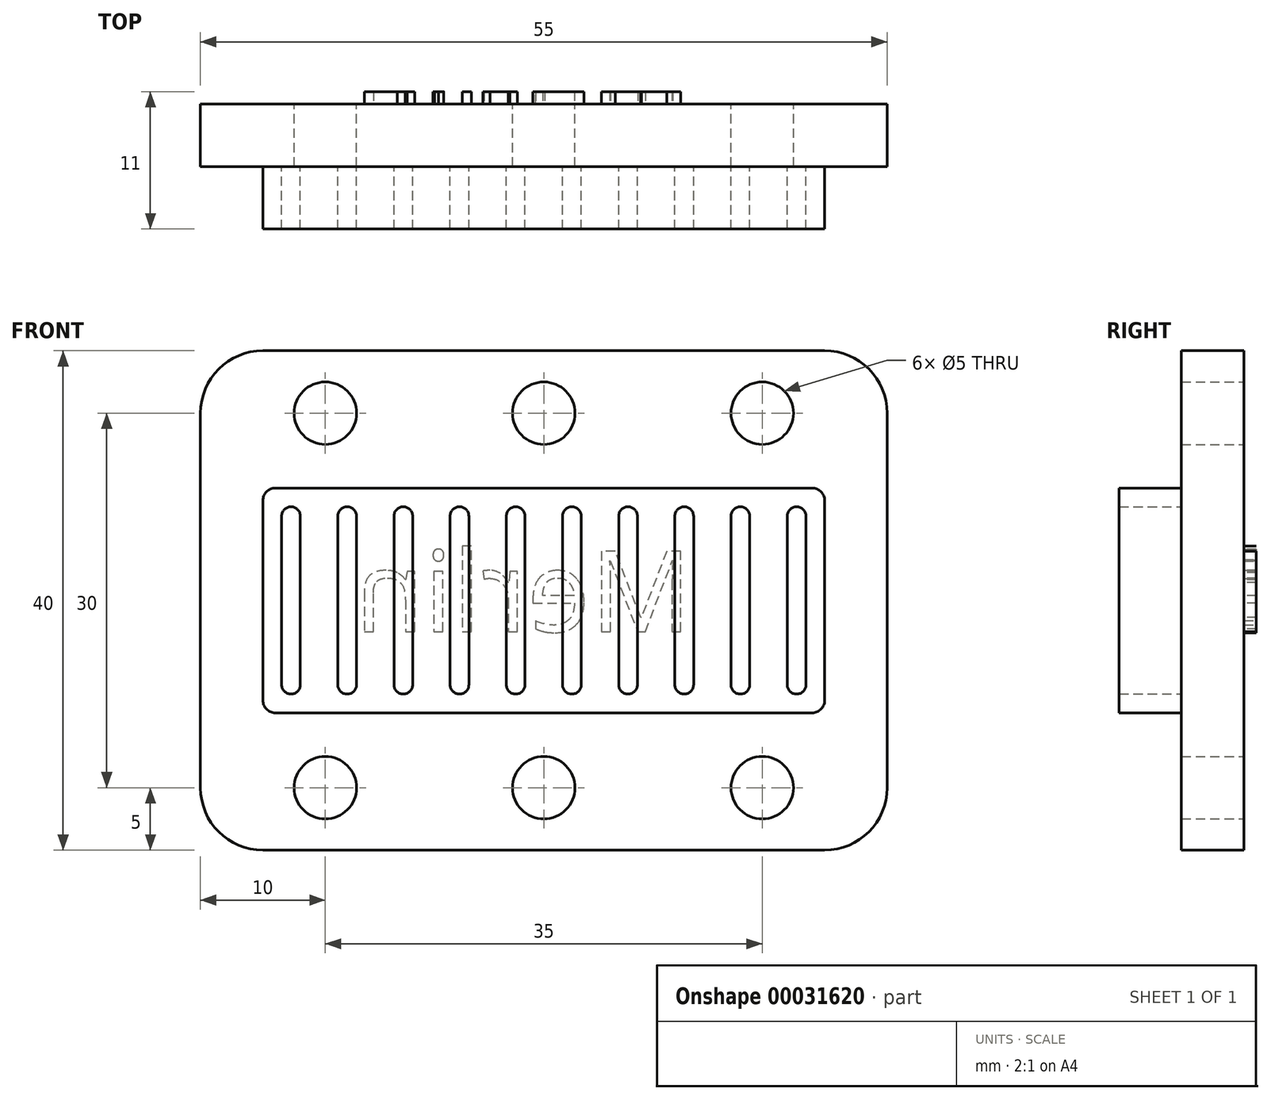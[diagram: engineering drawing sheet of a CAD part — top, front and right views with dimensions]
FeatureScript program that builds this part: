
annotation { "Feature Type Name" : "Feature", "Feature Type Description" : "" }
export const myFeature = defineFeature(function(context is Context, id is Id, definition is map)
    precondition{}
    {
        {
            var Q0;
            Q0=qCreatedBy(makeId("Front.planeOp"),FACE);
            var sketch = newSketch(context, id + "F0", { "sketchPlane" : qUnion([Q0])});
            skLineSegment(sketch, "E0.bottom", {"start": v(-5, 0) * mm, "end": v(-50, 0) * mm});
            skLineSegment(sketch, "E0.top", {"start": v(-5, 40) * mm, "end": v(-50, 40) * mm});
            skLineSegment(sketch, "E0.left", {"start": v(0, 5) * mm, "end": v(0, 35) * mm});
            skLineSegment(sketch, "E0.right", {"start": v(-55, 5) * mm, "end": v(-55, 35) * mm});
            skCircle(sketch, "E1", {"center": v(-45, 35) * mm, "radius": 2.5 * mm});
            skLineSegment(sketch, "E2", {"start": v(-67.85, 20) * mm, "end": v(10.82, 20) * mm, "construction": true});
            skCircle(sketch, "E3.MirrorC", {"center": v(-45, 5) * mm, "radius": 2.5 * mm});
            skCircle(sketch, "E4", {"center": v(-27.5, 35) * mm, "radius": 2.5 * mm});
            skCircle(sketch, "E5", {"center": v(-10, 35) * mm, "radius": 2.5 * mm});
            skCircle(sketch, "E6.MirrorC", {"center": v(-27.5, 5) * mm, "radius": 2.5 * mm});
            skCircle(sketch, "E7.MirrorC", {"center": v(-10, 5) * mm, "radius": 2.5 * mm});
            skPoint(sketch, "E8.visualSharp", {"position": v(-55, 40) * mm});
            skArc(sketch, "E8.filletArc", {"start": v(-50, 40) * mm, "mid": v(-53.54, 38.54) * mm, "end": v(-55, 35) * mm});
            skPoint(sketch, "E9.visualSharp", {"position": v(-55, 0) * mm});
            skArc(sketch, "E9.filletArc", {"start": v(-55, 5) * mm, "mid": v(-53.54, 1.46) * mm, "end": v(-50, 0) * mm});
            skPoint(sketch, "E10.visualSharp", {"position": v(0, 0) * mm});
            skArc(sketch, "E10.filletArc", {"start": v(-5, 0) * mm, "mid": v(-1.46, 1.46) * mm, "end": v(0, 5) * mm});
            skPoint(sketch, "E11.visualSharp", {"position": v(0, 40) * mm});
            skArc(sketch, "E11.filletArc", {"start": v(0, 35) * mm, "mid": v(-1.46, 38.54) * mm, "end": v(-5, 40) * mm});
            skSolve(sketch);
        }
        {
            var Q0;
            Q0 = qSketchRegion(id + "F0", true);
            extrude(context, id + "F1", {"entities" : qUnion([Q0]), "depth" : 5 * mm});
        }
        {
            var Q0;
            Q0=makeQuery(id+"F1.opExtrude","CAP_FACE",FACE,{"disambiguationData":[OSD([sQuery(id+"F0.wireOp",EDGE,"E0.bottom"),sQuery(id+"F0.wireOp",EDGE,"E0.top"),sQuery(id+"F0.wireOp",EDGE,"E0.left"),sQuery(id+"F0.wireOp",EDGE,"E0.right"),sQuery(id+"F0.wireOp",EDGE,"E1"),sQuery(id+"F0.wireOp",EDGE,"E3.MirrorC"),sQuery(id+"F0.wireOp",EDGE,"E4"),sQuery(id+"F0.wireOp",EDGE,"E5"),sQuery(id+"F0.wireOp",EDGE,"E6.MirrorC"),sQuery(id+"F0.wireOp",EDGE,"E7.MirrorC"),sQuery(id+"F0.wireOp",EDGE,"E8.filletArc"),sQuery(id+"F0.wireOp",EDGE,"E9.filletArc"),sQuery(id+"F0.wireOp",EDGE,"E10.filletArc"),sQuery(id+"F0.wireOp",EDGE,"E11.filletArc")])],"isStart":true});
            var sketch = newSketch(context, id + "F2", { "sketchPlane" : qUnion([Q0])});
            skText(sketch, "E12", { "text": "Merlin", "fontName": "OpenSans-Regular.ttf"});
            const initialGuessF2  = {"E12": [0.01564, 0.0175, 1, 0, 0.00649]};
            skSetInitialGuess(sketch, initialGuessF2);
            skSolve(sketch);
        }
        {
            var Q0;
            Q0 = qSketchRegion(id + "F2", true);
            extrude(context, id + "F3", {"entities" : qUnion([Q0]), "operationType" : NewBodyOperationType.ADD, "depth" : 1 * mm});
        }
        {
            var Q0;
            Q0=makeQuery(id+"F1.opExtrude","CAP_FACE",FACE,{"disambiguationData":[OSD([sQuery(id+"F0.wireOp",EDGE,"E0.bottom"),sQuery(id+"F0.wireOp",EDGE,"E0.top"),sQuery(id+"F0.wireOp",EDGE,"E0.left"),sQuery(id+"F0.wireOp",EDGE,"E0.right"),sQuery(id+"F0.wireOp",EDGE,"E1"),sQuery(id+"F0.wireOp",EDGE,"E3.MirrorC"),sQuery(id+"F0.wireOp",EDGE,"E4"),sQuery(id+"F0.wireOp",EDGE,"E5"),sQuery(id+"F0.wireOp",EDGE,"E6.MirrorC"),sQuery(id+"F0.wireOp",EDGE,"E7.MirrorC"),sQuery(id+"F0.wireOp",EDGE,"E8.filletArc"),sQuery(id+"F0.wireOp",EDGE,"E9.filletArc"),sQuery(id+"F0.wireOp",EDGE,"E10.filletArc"),sQuery(id+"F0.wireOp",EDGE,"E11.filletArc")])],"isStart":false});
            var sketch = newSketch(context, id + "F4", { "sketchPlane" : qUnion([Q0])});
            skLineSegment(sketch, "E13.bottom", {"start": v(-49, 29) * mm, "end": v(-6, 29) * mm});
            skLineSegment(sketch, "E13.top", {"start": v(-49, 11) * mm, "end": v(-6, 11) * mm});
            skLineSegment(sketch, "E13.left", {"start": v(-50, 28) * mm, "end": v(-50, 12) * mm});
            skLineSegment(sketch, "E13.right", {"start": v(-5, 28) * mm, "end": v(-5, 12) * mm});
            skLineSegment(sketch, "E14.bottom", {"start": v(-47.75, 27.5) * mm, "end": v(-47.75, 27.5) * mm});
            skLineSegment(sketch, "E14.top", {"start": v(-47.75, 12.5) * mm, "end": v(-47.75, 12.5) * mm});
            skLineSegment(sketch, "E14.left", {"start": v(-48.5, 26.75) * mm, "end": v(-48.5, 13.25) * mm});
            skLineSegment(sketch, "E14.right", {"start": v(-47, 26.75) * mm, "end": v(-47, 13.25) * mm});
            skPoint(sketch, "E15.visualSharp", {"position": v(-5, 29) * mm});
            skArc(sketch, "E15.filletArc", {"start": v(-5, 28) * mm, "mid": v(-5.3, 28.7) * mm, "end": v(-6, 29) * mm});
            skPoint(sketch, "E16.visualSharp", {"position": v(-5, 11) * mm});
            skArc(sketch, "E16.filletArc", {"start": v(-6, 11) * mm, "mid": v(-5.3, 11.3) * mm, "end": v(-5, 12) * mm});
            skPoint(sketch, "E17.visualSharp", {"position": v(-50, 11) * mm});
            skArc(sketch, "E17.filletArc", {"start": v(-50, 12) * mm, "mid": v(-49.7, 11.3) * mm, "end": v(-49, 11) * mm});
            skPoint(sketch, "E18.visualSharp", {"position": v(-50, 29) * mm});
            skArc(sketch, "E18.filletArc", {"start": v(-49, 29) * mm, "mid": v(-49.7, 28.7) * mm, "end": v(-50, 28) * mm});
            skPoint(sketch, "E19.visualSharp", {"position": v(-47, 27.5) * mm});
            skArc(sketch, "E19.filletArc", {"start": v(-47, 26.75) * mm, "mid": v(-47.22, 27.28) * mm, "end": v(-47.75, 27.5) * mm});
            skPoint(sketch, "E20.visualSharp", {"position": v(-48.5, 27.5) * mm});
            skArc(sketch, "E20.filletArc", {"start": v(-47.75, 27.5) * mm, "mid": v(-48.28, 27.28) * mm, "end": v(-48.5, 26.75) * mm});
            skPoint(sketch, "E21.visualSharp", {"position": v(-48.5, 12.5) * mm});
            skArc(sketch, "E21.filletArc", {"start": v(-48.5, 13.25) * mm, "mid": v(-48.28, 12.72) * mm, "end": v(-47.75, 12.5) * mm});
            skPoint(sketch, "E22.visualSharp", {"position": v(-47, 12.5) * mm});
            skArc(sketch, "E22.filletArc", {"start": v(-47.75, 12.5) * mm, "mid": v(-47.22, 12.72) * mm, "end": v(-47, 13.25) * mm});
            skLineSegment(sketch, "E23.1.0.0", {"start": v(-44, 26.75) * mm, "end": v(-44, 13.25) * mm});
            skArc(sketch, "E23.1.0.1", {"start": v(-43.25, 27.5) * mm, "mid": v(-43.78, 27.28) * mm, "end": v(-44, 26.75) * mm});
            skArc(sketch, "E23.1.0.2", {"start": v(-42.5, 26.75) * mm, "mid": v(-42.72, 27.28) * mm, "end": v(-43.25, 27.5) * mm});
            skLineSegment(sketch, "E23.1.0.3", {"start": v(-42.5, 26.75) * mm, "end": v(-42.5, 13.25) * mm});
            skArc(sketch, "E23.1.0.4", {"start": v(-43.25, 12.5) * mm, "mid": v(-42.72, 12.72) * mm, "end": v(-42.5, 13.25) * mm});
            skArc(sketch, "E23.1.0.5", {"start": v(-44, 13.25) * mm, "mid": v(-43.78, 12.72) * mm, "end": v(-43.25, 12.5) * mm});
            skLineSegment(sketch, "E23.2.0.0", {"start": v(-39.5, 26.75) * mm, "end": v(-39.5, 13.25) * mm});
            skArc(sketch, "E23.2.0.1", {"start": v(-38.75, 27.5) * mm, "mid": v(-39.28, 27.28) * mm, "end": v(-39.5, 26.75) * mm});
            skArc(sketch, "E23.2.0.2", {"start": v(-38, 26.75) * mm, "mid": v(-38.22, 27.28) * mm, "end": v(-38.75, 27.5) * mm});
            skLineSegment(sketch, "E23.2.0.3", {"start": v(-38, 26.75) * mm, "end": v(-38, 13.25) * mm});
            skArc(sketch, "E23.2.0.4", {"start": v(-38.75, 12.5) * mm, "mid": v(-38.22, 12.72) * mm, "end": v(-38, 13.25) * mm});
            skArc(sketch, "E23.2.0.5", {"start": v(-39.5, 13.25) * mm, "mid": v(-39.28, 12.72) * mm, "end": v(-38.75, 12.5) * mm});
            skLineSegment(sketch, "E23.direction1", {"start": v(-48.5, 13.25) * mm, "end": v(-44, 13.25) * mm, "construction": true});
            skLineSegment(sketch, "E24.0.3.0", {"start": v(-35, 26.75) * mm, "end": v(-35, 13.25) * mm});
            skArc(sketch, "E24.3.3.0", {"start": v(-34.25, 27.5) * mm, "mid": v(-34.78, 27.28) * mm, "end": v(-35, 26.75) * mm});
            skArc(sketch, "E24.7.3.0", {"start": v(-33.5, 26.75) * mm, "mid": v(-33.72, 27.28) * mm, "end": v(-34.25, 27.5) * mm});
            skLineSegment(sketch, "E24.11.3.0", {"start": v(-33.5, 26.75) * mm, "end": v(-33.5, 13.25) * mm});
            skArc(sketch, "E24.14.3.0", {"start": v(-34.25, 12.5) * mm, "mid": v(-33.72, 12.72) * mm, "end": v(-33.5, 13.25) * mm});
            skArc(sketch, "E24.18.3.0", {"start": v(-35, 13.25) * mm, "mid": v(-34.78, 12.72) * mm, "end": v(-34.25, 12.5) * mm});
            skLineSegment(sketch, "E24.0.4.0", {"start": v(-30.5, 26.75) * mm, "end": v(-30.5, 13.25) * mm});
            skArc(sketch, "E24.3.4.0", {"start": v(-29.75, 27.5) * mm, "mid": v(-30.28, 27.28) * mm, "end": v(-30.5, 26.75) * mm});
            skArc(sketch, "E24.7.4.0", {"start": v(-29, 26.75) * mm, "mid": v(-29.22, 27.28) * mm, "end": v(-29.75, 27.5) * mm});
            skLineSegment(sketch, "E24.11.4.0", {"start": v(-29, 26.75) * mm, "end": v(-29, 13.25) * mm});
            skArc(sketch, "E24.14.4.0", {"start": v(-29.75, 12.5) * mm, "mid": v(-29.22, 12.72) * mm, "end": v(-29, 13.25) * mm});
            skArc(sketch, "E24.18.4.0", {"start": v(-30.5, 13.25) * mm, "mid": v(-30.28, 12.72) * mm, "end": v(-29.75, 12.5) * mm});
            skLineSegment(sketch, "E24.0.5.0", {"start": v(-26, 26.75) * mm, "end": v(-26, 13.25) * mm});
            skArc(sketch, "E24.3.5.0", {"start": v(-25.25, 27.5) * mm, "mid": v(-25.78, 27.28) * mm, "end": v(-26, 26.75) * mm});
            skArc(sketch, "E24.7.5.0", {"start": v(-24.5, 26.75) * mm, "mid": v(-24.72, 27.28) * mm, "end": v(-25.25, 27.5) * mm});
            skLineSegment(sketch, "E24.11.5.0", {"start": v(-24.5, 26.75) * mm, "end": v(-24.5, 13.25) * mm});
            skArc(sketch, "E24.14.5.0", {"start": v(-25.25, 12.5) * mm, "mid": v(-24.72, 12.72) * mm, "end": v(-24.5, 13.25) * mm});
            skArc(sketch, "E24.18.5.0", {"start": v(-26, 13.25) * mm, "mid": v(-25.78, 12.72) * mm, "end": v(-25.25, 12.5) * mm});
            skLineSegment(sketch, "E24.0.6.0", {"start": v(-21.5, 26.75) * mm, "end": v(-21.5, 13.25) * mm});
            skArc(sketch, "E24.3.6.0", {"start": v(-20.75, 27.5) * mm, "mid": v(-21.28, 27.28) * mm, "end": v(-21.5, 26.75) * mm});
            skArc(sketch, "E24.7.6.0", {"start": v(-20, 26.75) * mm, "mid": v(-20.22, 27.28) * mm, "end": v(-20.75, 27.5) * mm});
            skLineSegment(sketch, "E24.11.6.0", {"start": v(-20, 26.75) * mm, "end": v(-20, 13.25) * mm});
            skArc(sketch, "E24.14.6.0", {"start": v(-20.75, 12.5) * mm, "mid": v(-20.22, 12.72) * mm, "end": v(-20, 13.25) * mm});
            skArc(sketch, "E24.18.6.0", {"start": v(-21.5, 13.25) * mm, "mid": v(-21.28, 12.72) * mm, "end": v(-20.75, 12.5) * mm});
            skLineSegment(sketch, "E24.0.7.0", {"start": v(-17, 26.75) * mm, "end": v(-17, 13.25) * mm});
            skArc(sketch, "E24.3.7.0", {"start": v(-16.25, 27.5) * mm, "mid": v(-16.78, 27.28) * mm, "end": v(-17, 26.75) * mm});
            skArc(sketch, "E24.7.7.0", {"start": v(-15.5, 26.75) * mm, "mid": v(-15.72, 27.28) * mm, "end": v(-16.25, 27.5) * mm});
            skLineSegment(sketch, "E24.11.7.0", {"start": v(-15.5, 26.75) * mm, "end": v(-15.5, 13.25) * mm});
            skArc(sketch, "E24.14.7.0", {"start": v(-16.25, 12.5) * mm, "mid": v(-15.72, 12.72) * mm, "end": v(-15.5, 13.25) * mm});
            skArc(sketch, "E24.18.7.0", {"start": v(-17, 13.25) * mm, "mid": v(-16.78, 12.72) * mm, "end": v(-16.25, 12.5) * mm});
            skLineSegment(sketch, "E24.0.8.0", {"start": v(-12.5, 26.75) * mm, "end": v(-12.5, 13.25) * mm});
            skArc(sketch, "E24.3.8.0", {"start": v(-11.75, 27.5) * mm, "mid": v(-12.28, 27.28) * mm, "end": v(-12.5, 26.75) * mm});
            skArc(sketch, "E24.7.8.0", {"start": v(-11, 26.75) * mm, "mid": v(-11.22, 27.28) * mm, "end": v(-11.75, 27.5) * mm});
            skLineSegment(sketch, "E24.11.8.0", {"start": v(-11, 26.75) * mm, "end": v(-11, 13.25) * mm});
            skArc(sketch, "E24.14.8.0", {"start": v(-11.75, 12.5) * mm, "mid": v(-11.22, 12.72) * mm, "end": v(-11, 13.25) * mm});
            skArc(sketch, "E24.18.8.0", {"start": v(-12.5, 13.25) * mm, "mid": v(-12.28, 12.72) * mm, "end": v(-11.75, 12.5) * mm});
            skLineSegment(sketch, "E24.0.9.0", {"start": v(-8, 26.75) * mm, "end": v(-8, 13.25) * mm});
            skArc(sketch, "E24.3.9.0", {"start": v(-7.25, 27.5) * mm, "mid": v(-7.78, 27.28) * mm, "end": v(-8, 26.75) * mm});
            skArc(sketch, "E24.7.9.0", {"start": v(-6.5, 26.75) * mm, "mid": v(-6.72, 27.28) * mm, "end": v(-7.25, 27.5) * mm});
            skLineSegment(sketch, "E24.11.9.0", {"start": v(-6.5, 26.75) * mm, "end": v(-6.5, 13.25) * mm});
            skArc(sketch, "E24.14.9.0", {"start": v(-7.25, 12.5) * mm, "mid": v(-6.72, 12.72) * mm, "end": v(-6.5, 13.25) * mm});
            skArc(sketch, "E24.18.9.0", {"start": v(-8, 13.25) * mm, "mid": v(-7.78, 12.72) * mm, "end": v(-7.25, 12.5) * mm});
            skSolve(sketch);
        }
        {
            var Q0;
            Q0 = qSketchRegion(id + "F4", true);
            extrude(context, id + "F5", {"entities" : qUnion([Q0]), "operationType" : NewBodyOperationType.ADD, "depth" : 5 * mm});
        }
    });
